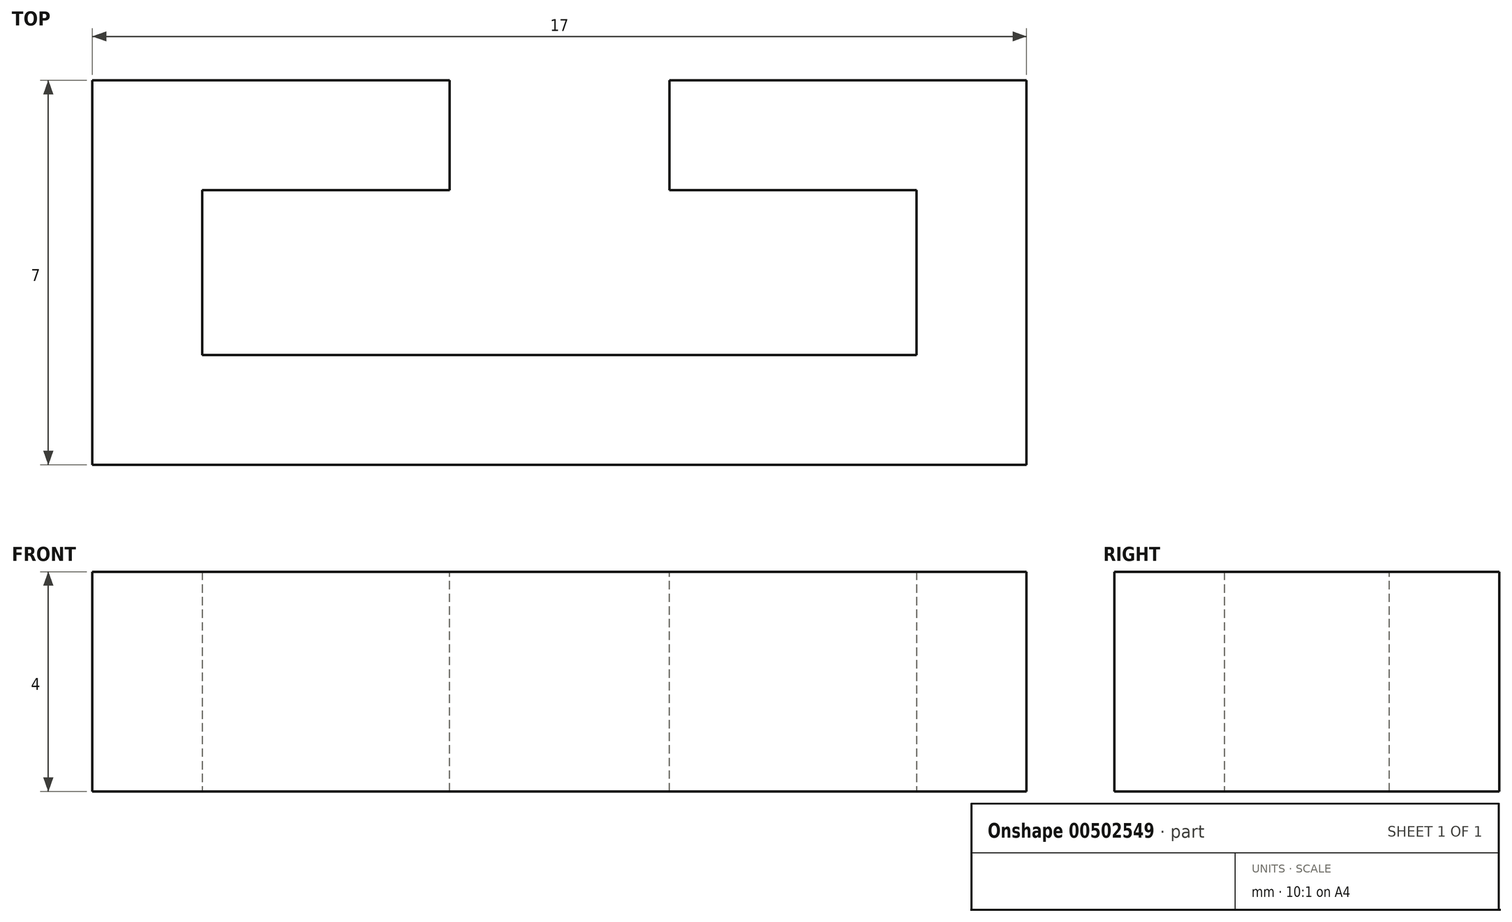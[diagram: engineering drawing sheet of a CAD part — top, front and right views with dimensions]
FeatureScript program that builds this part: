
annotation { "Feature Type Name" : "Feature", "Feature Type Description" : "" }
export const myFeature = defineFeature(function(context is Context, id is Id, definition is map)
    precondition{}
    {
        {
            var Q0;
            Q0=qCreatedBy(makeId("Top.planeOp"),FACE);
            var sketch = newSketch(context, id + "F0", { "sketchPlane" : qUnion([Q0])});
            skLineSegment(sketch, "E0.bottom", {"start": v(-6.5, 1.5) * mm, "end": v(6.5, 1.5) * mm});
            skLineSegment(sketch, "E0.top", {"start": v(-6.5, -1.5) * mm, "end": v(6.5, -1.5) * mm});
            skLineSegment(sketch, "E0.left", {"start": v(-6.5, 1.5) * mm, "end": v(-6.5, -1.5) * mm});
            skLineSegment(sketch, "E0.right", {"start": v(6.5, 1.5) * mm, "end": v(6.5, -1.5) * mm});
            skLineSegment(sketch, "E1.bottom", {"start": v(-8.5, 3.5) * mm, "end": v(8.5, 3.5) * mm});
            skLineSegment(sketch, "E1.top", {"start": v(-8.5, -3.5) * mm, "end": v(8.5, -3.5) * mm});
            skLineSegment(sketch, "E1.left", {"start": v(-8.5, 3.5) * mm, "end": v(-8.5, -3.5) * mm});
            skLineSegment(sketch, "E1.right", {"start": v(8.5, 3.5) * mm, "end": v(8.5, -3.5) * mm});
            skSolve(sketch);
        }
        {
            var Q0;
            Q0=makeQuery(id+"F0.imprint","IMPRINT",FACE,{"disambiguationData":[TD([[makeQuery(id+"F0.imprint","IMPRINT",EDGE,{"derivedFrom":sQuery(id+"F0.wireOp",EDGE,"E0.bottom")}),1.0]])]});
            extrude(context, id + "F1", {"entities" : qUnion([Q0]), "depth" : 4 * mm});
        }
        {
            var Q0;
            Q0=makeQuery(id+"F1.opExtrude","CAP_FACE",FACE,{"disambiguationData":[OSD([sQuery(id+"F0.wireOp",EDGE,"E0.bottom"),sQuery(id+"F0.wireOp",EDGE,"E0.top"),sQuery(id+"F0.wireOp",EDGE,"E0.left"),sQuery(id+"F0.wireOp",EDGE,"E0.right"),sQuery(id+"F0.wireOp",EDGE,"E1.bottom"),sQuery(id+"F0.wireOp",EDGE,"E1.top"),sQuery(id+"F0.wireOp",EDGE,"E1.left"),sQuery(id+"F0.wireOp",EDGE,"E1.right")])],"isStart":false});
            var sketch = newSketch(context, id + "F2", { "sketchPlane" : qUnion([Q0])});
            skLineSegment(sketch, "E2.bottom", {"start": v(-2, 3.5) * mm, "end": v(2, 3.5) * mm});
            skLineSegment(sketch, "E2.top", {"start": v(-2, 1.5) * mm, "end": v(2, 1.5) * mm});
            skLineSegment(sketch, "E2.left", {"start": v(-2, 3.5) * mm, "end": v(-2, 1.5) * mm});
            skLineSegment(sketch, "E2.right", {"start": v(2, 3.5) * mm, "end": v(2, 1.5) * mm});
            skSolve(sketch);
        }
        {
            var Q0;
            Q0=makeQuery(id+"F2.imprint","IMPRINT",FACE,{"disambiguationData":[TD([[makeQuery(id+"F2.imprint","IMPRINT",EDGE,{"derivedFrom":sQuery(id+"F2.wireOp",EDGE,"E2.bottom")}),-1.0]])]});
            extrude(context, id + "F3", {"entities" : qUnion([Q0]), "operationType" : NewBodyOperationType.REMOVE, "oppositeDirection" : true, "depth" : 25 * mm});
        }
    });
